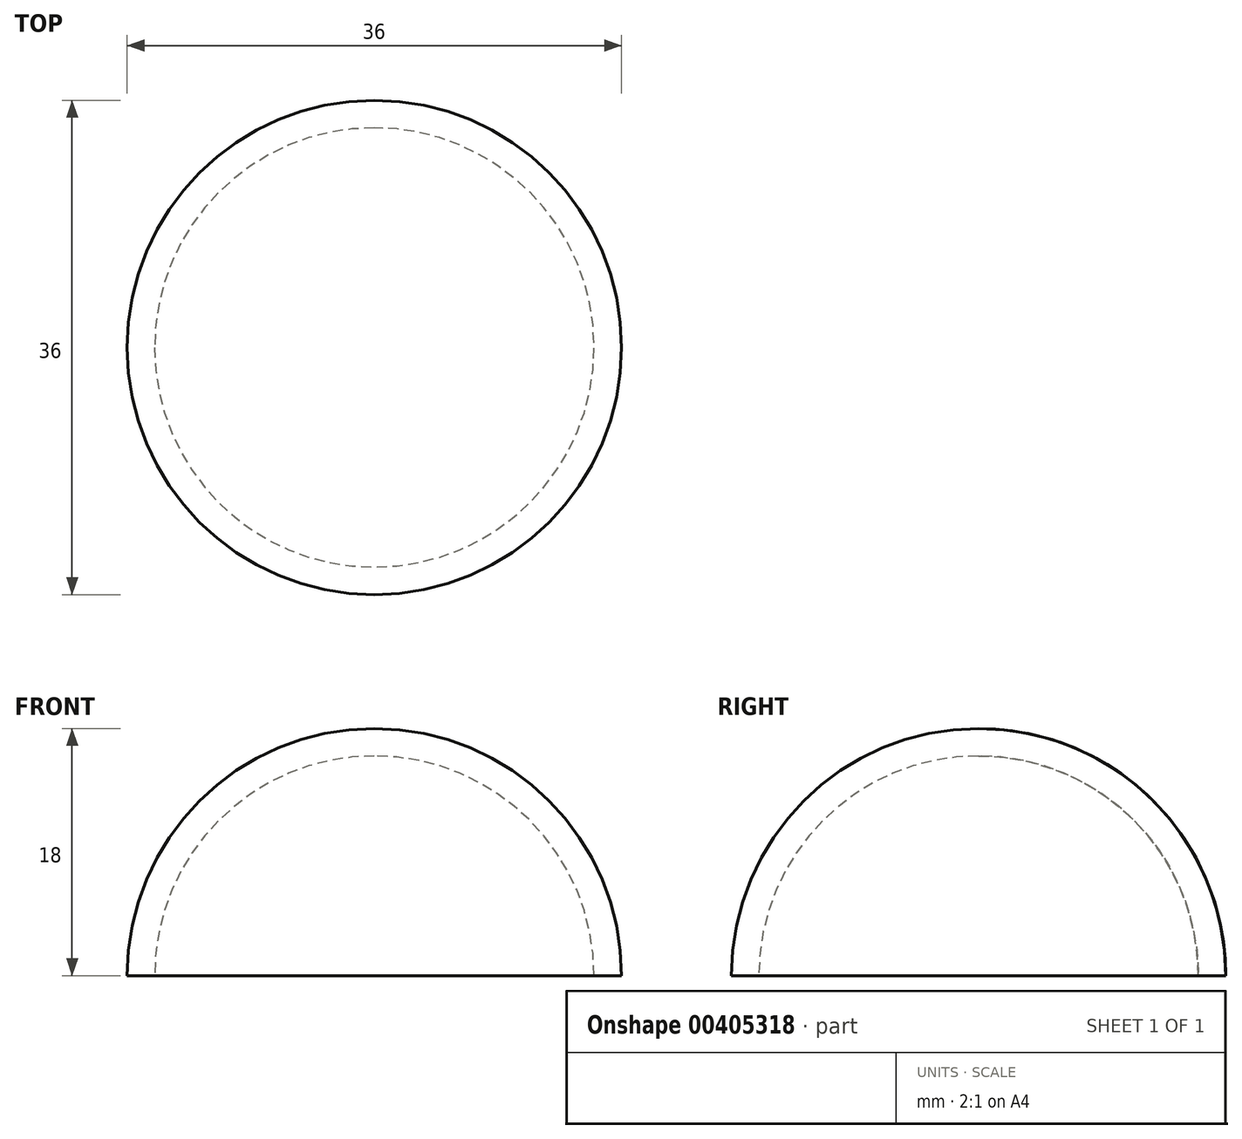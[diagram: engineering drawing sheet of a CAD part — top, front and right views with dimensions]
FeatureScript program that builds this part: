
annotation { "Feature Type Name" : "Feature", "Feature Type Description" : "" }
export const myFeature = defineFeature(function(context is Context, id is Id, definition is map)
    precondition{}
    {
        {
            var Q0;
            Q0=qCreatedBy(makeId("Right.planeOp"),FACE);
            var sketch = newSketch(context, id + "F0", { "sketchPlane" : qUnion([Q0])});
            skArc(sketch, "E0", {"start": v(16, 0) * mm, "mid": v(11.31, 11.31) * mm, "end": v(0, 16) * mm});
            skArc(sketch, "E1", {"start": v(18, 0) * mm, "mid": v(12.73, 12.73) * mm, "end": v(0, 18) * mm});
            skLineSegment(sketch, "E2", {"start": v(0, 16) * mm, "end": v(0, 18) * mm});
            skLineSegment(sketch, "E3", {"start": v(16, 0) * mm, "end": v(18, 0) * mm});
            skSolve(sketch);
        }
        {
            var Q0;
            Q0=makeQuery(id+"F0.imprint","IMPRINT",FACE,{"disambiguationData":[TD([[makeQuery(id+"F0.imprint","IMPRINT",EDGE,{"derivedFrom":sQuery(id+"F0.wireOp",EDGE,"E0")}),-1.0]])]});
            var Q1;
            Q1=sQuery(id+"F0.wireOp",EDGE,"E2");
            revolve(context, id + "F1", {"entities" : qUnion([Q0]), "axis" : qUnion([Q1]), "revolveType" : RevolveType.FULL});
        }
    });
